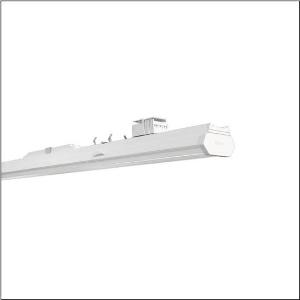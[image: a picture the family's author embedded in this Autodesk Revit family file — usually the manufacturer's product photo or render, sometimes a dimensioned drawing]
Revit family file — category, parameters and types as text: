
# Revit family: licross_r__11_protected_mo_51tp11cn49xg_312d
name_source: partatom
category: Lighting Fixtures
units: mm (PartAtom-declared; Revit-internal decimal feet)

## family parameters
Cut with Voids When Loaded = No
Host = Face
Light Source = No
Part Type = Normal
Room Calculation Point = No
Round Connector Dimension = Use Diameter
Shared = No

## types (1)
- --- (1 x LED, 9030 lm, 49.4 W, 4000K)
    Apparent Load = 49 VA
    CIE Flux Codes = 83 94 98 100 100
    Color Rendering = 80
    Color Temperature = 4000K
    Default Elevation = 1800 mm
    Description = Licross® 11 Protected MO, luminaire insert, of sheet steel, galvanised, coil coated, white, length: 1.500mm, width: 90mm, height: 101mm, LED rated luminous flux: 9.030lm, light colour: 840, control gear: ON/OFF Multilumen, CLOi, with plug, 3-pole, with phase selection, mains connection: 220..240V, AC, 50/60Hz, start of lifetime: 49W, end of service life: 55W, halogen-free wiring, primary light control with lens, of plastic, primary optical cover: cover, of PMMA, light emission: direct distribution, primary light characteristic: symmetric, protection rating (complete): IP64, insulation class (complete): insulation class I (protective earthing), certification: CE, ENEC, VDE, UKCA, protection symbol: D if used in an environment with conductive dust loads with corresponding accessories, impact resistance: IK06, permissible ambient temperature for indoor applications: -35..+40°C, corresponds to IFS (International Featured Standards) requirements for safety and quality in the food industry, reducing of maximum allowable ambient temperature of 5°C with ceiling mounting, LABS conformity tested according to VDMA 24364:2018-05, packaging unit: 1 piece
    Height = 92 mm
    Lamp = 1 x LED
    Lamp Light Flux = 9030 lm
    Lamp Power = 49.4 W
    Lamp count = 1
    Length = 1500 mm
    Luminous efficacy = 183 lm/W
    Manufacturer = Siteco
    ModVariant = No
    Model = 51TP11CN49XG
    Mounting Place = Ceiling
    Mounting Type = Pendant
    Number of Poles = 1
    OnlyDefault = Yes
    Power Factor = 1
    Product Name = Licross® 11 Protected MO
    Product group = luminaire insert
    ProductGroupID = 901
    Protection Class = Protection class I
    Protection Degree = IP 64
    RLX_Detail_Level = 1
    RLX_Emergency_Light_Flux = 0 lm
    RLX_Emergency_Type = 0
    RLX_Emergency_Type_DB = No
    RlxData = <blob elided: 21893 chars, md5=fba752f7>
    Socket = socket
    Standby Power = 0 W
    System Light Flux = 9030 lm
    System Power = 49 W
    Type Comments = factory setting: luminous flux: 100 % | (A | C | E) | 113 mA
    Type Image = l_1256148.jpg
    URL = http://relux.com
    VarID = @adj_019263
    Voltage = 0 V
    Weight = 0.00 kg
    Width = 88 mm

## geometry (parser evidence)
native form markers: Blend x4, Sweep x11
no freeform markers — native parametric forms only
